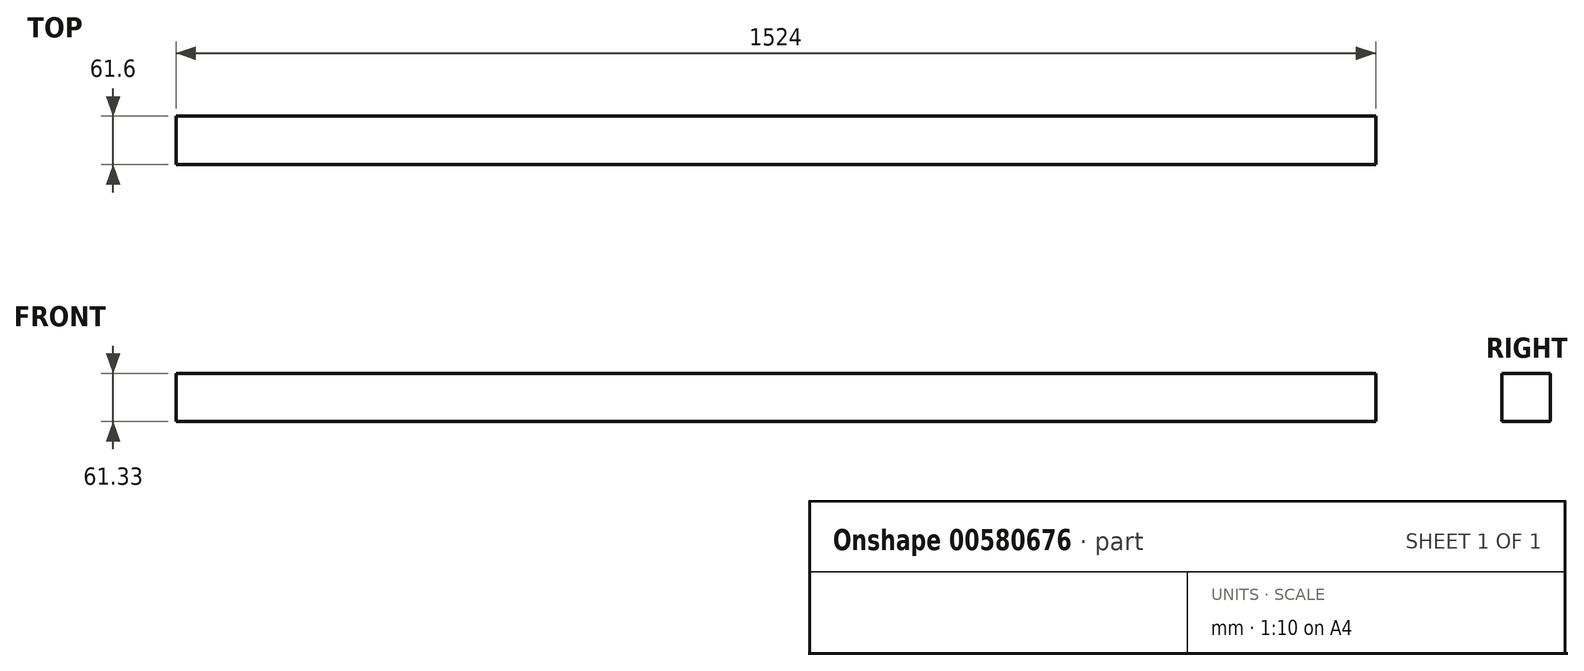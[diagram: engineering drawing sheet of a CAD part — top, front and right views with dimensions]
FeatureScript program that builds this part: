
annotation { "Feature Type Name" : "Feature", "Feature Type Description" : "" }
export const myFeature = defineFeature(function(context is Context, id is Id, definition is map)
    precondition{}
    {
        {
            var Q0;
            Q0=qCreatedBy(makeId("Right.planeOp"),FACE);
            var sketch = newSketch(context, id + "F0", { "sketchPlane" : qUnion([Q0])});
            skLineSegment(sketch, "E0.bottom", {"start": v(0, 0) * mm, "end": v(61.6, 0) * mm});
            skLineSegment(sketch, "E0.top", {"start": v(0, 61.33) * mm, "end": v(61.6, 61.33) * mm});
            skLineSegment(sketch, "E0.left", {"start": v(0, 0) * mm, "end": v(0, 61.33) * mm});
            skLineSegment(sketch, "E0.right", {"start": v(61.6, 0) * mm, "end": v(61.6, 61.33) * mm});
            skSolve(sketch);
        }
        {
            var Q0;
            Q0=makeQuery(id+"F0.imprint","IMPRINT",FACE,{"disambiguationData":[TD([[makeQuery(id+"F0.imprint","IMPRINT",EDGE,{"derivedFrom":sQuery(id+"F0.wireOp",EDGE,"E0.bottom")}),1.0]])]});
            extrude(context, id + "F1", {"entities" : qUnion([Q0]), "depth" : 1524 * mm, "offsetDistance" : 25.4 * mm});
        }
    });
